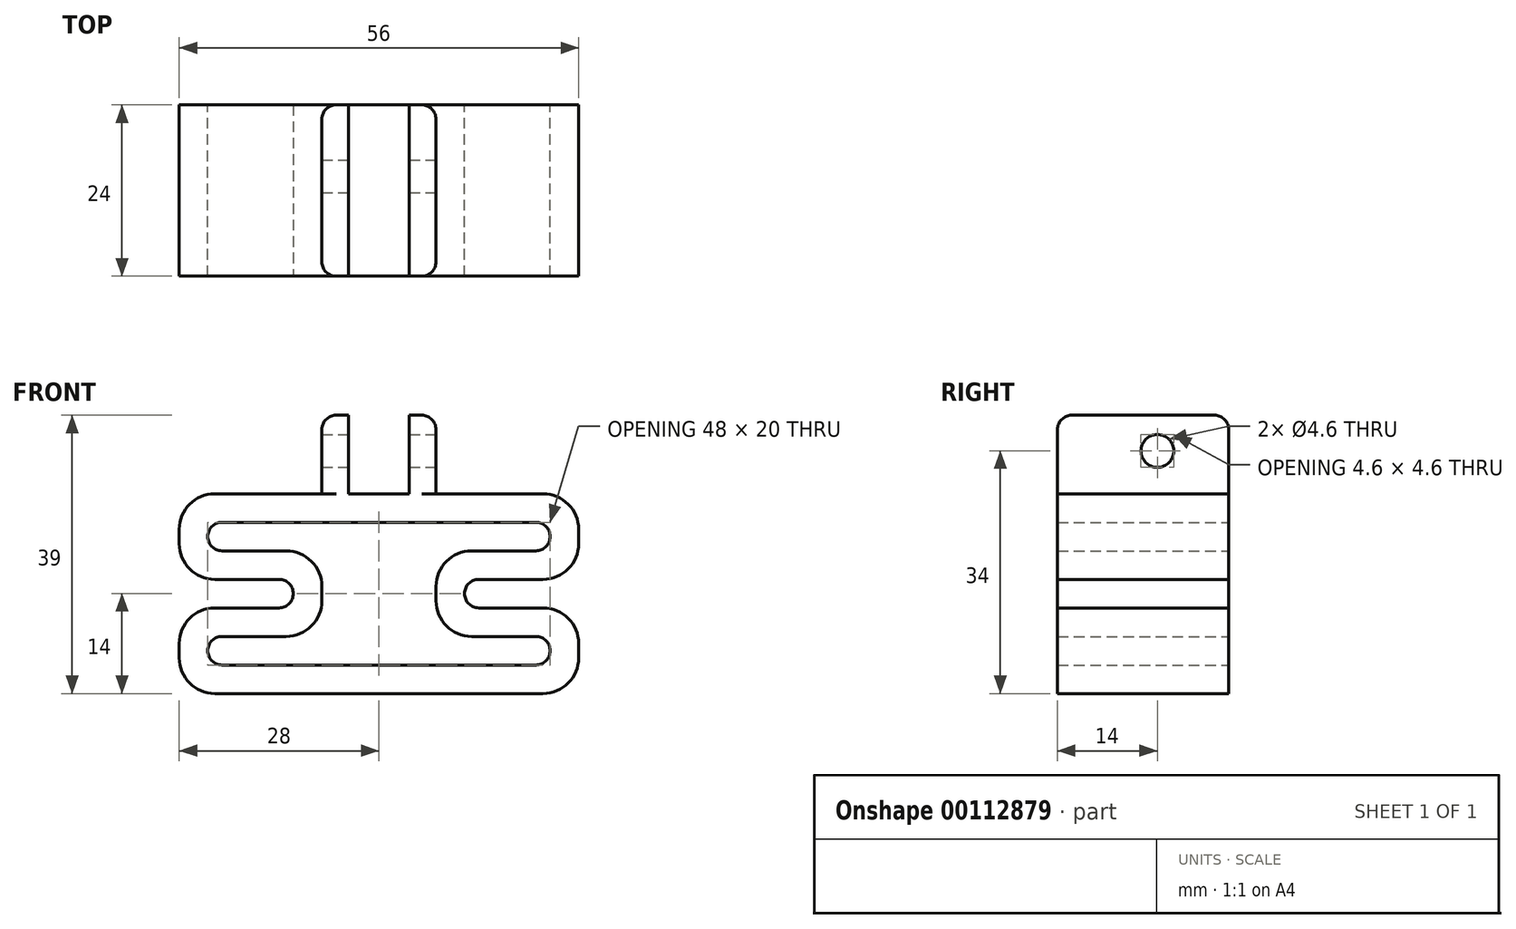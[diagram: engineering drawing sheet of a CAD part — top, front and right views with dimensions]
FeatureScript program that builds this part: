
annotation { "Feature Type Name" : "Feature", "Feature Type Description" : "" }
export const myFeature = defineFeature(function(context is Context, id is Id, definition is map)
    precondition{}
    {
        {
            var Q0;
            Q0=qCreatedBy(makeId("Front.planeOp"),FACE);
            var sketch = newSketch(context, id + "F0", { "sketchPlane" : qUnion([Q0])});
            skLineSegment(sketch, "E0.bottom", {"start": v(8, 11) * mm, "end": v(-8, 11) * mm});
            skLineSegment(sketch, "E0.left", {"start": v(8, 11) * mm, "end": v(8, -11) * mm});
            skLineSegment(sketch, "E0.right", {"start": v(-8, 11) * mm, "end": v(-8, 0) * mm});
            skPoint(sketch, "E0.middle", {"position": v(0, 0) * mm});
            skLineSegment(sketch, "E1.bottom", {"start": v(0, 0) * mm, "end": v(-28, 0) * mm});
            skLineSegment(sketch, "E1.top", {"start": v(0, -28) * mm, "end": v(-28, -28) * mm});
            skLineSegment(sketch, "E1.left", {"start": v(0, 0) * mm, "end": v(0, -28) * mm});
            skLineSegment(sketch, "E1.right", {"start": v(-28, 0) * mm, "end": v(-28, -12) * mm});
            skLineSegment(sketch, "E2", {"start": v(-8, -8) * mm, "end": v(-8, -20) * mm, "construction": true});
            skLineSegment(sketch, "E3.bottom", {"start": v(-8, -4) * mm, "end": v(-24, -4) * mm});
            skLineSegment(sketch, "E3.top", {"start": v(-8, -8) * mm, "end": v(-24, -8) * mm});
            skLineSegment(sketch, "E3.left", {"start": v(-8, -4) * mm, "end": v(-8, -8) * mm});
            skLineSegment(sketch, "E3.right", {"start": v(-24, -4) * mm, "end": v(-24, -8) * mm});
            skLineSegment(sketch, "E4.bottom", {"start": v(-28, -12) * mm, "end": v(-12, -12) * mm});
            skLineSegment(sketch, "E4.top", {"start": v(-28, -16) * mm, "end": v(-12, -16) * mm});
            skLineSegment(sketch, "E4.right", {"start": v(-12, -12) * mm, "end": v(-12, -16) * mm});
            skLineSegment(sketch, "E5.bottom", {"start": v(-8, -20) * mm, "end": v(-24, -20) * mm});
            skLineSegment(sketch, "E5.top", {"start": v(-8, -24) * mm, "end": v(-24, -24) * mm});
            skLineSegment(sketch, "E5.left", {"start": v(-8, -20) * mm, "end": v(-8, -24) * mm});
            skLineSegment(sketch, "E5.right", {"start": v(-24, -20) * mm, "end": v(-24, -24) * mm});
            skLineSegment(sketch, "E6.MirrorCS", {"start": v(0, 0) * mm, "end": v(28, 0) * mm});
            skLineSegment(sketch, "E7.MirrorCS", {"start": v(28, 0) * mm, "end": v(28, -12) * mm});
            skLineSegment(sketch, "E8.MirrorCS", {"start": v(28, -12) * mm, "end": v(12, -12) * mm});
            skLineSegment(sketch, "E9.MirrorCS", {"start": v(12, -12) * mm, "end": v(12, -16) * mm});
            skLineSegment(sketch, "E10.MirrorCS", {"start": v(28, -16) * mm, "end": v(12, -16) * mm});
            skLineSegment(sketch, "E11.MirrorCS", {"start": v(8, -20) * mm, "end": v(24, -20) * mm});
            skLineSegment(sketch, "E12.MirrorCS", {"start": v(24, -20) * mm, "end": v(24, -24) * mm});
            skLineSegment(sketch, "E13.MirrorCS", {"start": v(8, -24) * mm, "end": v(24, -24) * mm});
            skLineSegment(sketch, "E14.MirrorCS", {"start": v(0, -28) * mm, "end": v(28, -28) * mm});
            skLineSegment(sketch, "E15.MirrorCS", {"start": v(8, -4) * mm, "end": v(24, -4) * mm});
            skLineSegment(sketch, "E16.MirrorCS", {"start": v(24, -4) * mm, "end": v(24, -8) * mm});
            skLineSegment(sketch, "E17.MirrorCS", {"start": v(8, -8) * mm, "end": v(24, -8) * mm});
            skLineSegment(sketch, "E18.MirrorCS", {"start": v(8, -8) * mm, "end": v(8, -20) * mm, "construction": true});
            skLineSegment(sketch, "E19", {"start": v(-8, -4) * mm, "end": v(8, -4) * mm});
            skLineSegment(sketch, "E20", {"start": v(-8, -11) * mm, "end": v(-8, -20) * mm});
            skLineSegment(sketch, "E21", {"start": v(-8, -24) * mm, "end": v(8, -24) * mm});
            skLineSegment(sketch, "E22", {"start": v(8, -20) * mm, "end": v(8, -11) * mm});
            skPoint(sketch, "E23.orphan", {"position": v(-8, 0) * mm});
            skLineSegment(sketch, "E24.trimOffspring", {"start": v(-8, -24) * mm, "end": v(-8, -28) * mm, "construction": true});
            skLineSegment(sketch, "E25.trimOffspring", {"start": v(8, -24) * mm, "end": v(8, -28) * mm, "construction": true});
            skLineSegment(sketch, "E26.trimOffspring", {"start": v(-8, -4) * mm, "end": v(-8, -11) * mm});
            skPoint(sketch, "E27.orphan", {"position": v(8, 0) * mm});
            skLineSegment(sketch, "E28.trimOffspring", {"start": v(-28, -16) * mm, "end": v(-28, -28) * mm});
            skLineSegment(sketch, "E29.trimOffspring", {"start": v(28, -16) * mm, "end": v(28, -28) * mm});
            skLineSegment(sketch, "E30.bottom", {"start": v(-4.25, 0) * mm, "end": v(4.25, 0) * mm});
            skLineSegment(sketch, "E30.top", {"start": v(-4.25, 22) * mm, "end": v(4.25, 22) * mm});
            skLineSegment(sketch, "E30.left", {"start": v(-4.25, 0) * mm, "end": v(-4.25, 22) * mm});
            skLineSegment(sketch, "E30.right", {"start": v(4.25, 0) * mm, "end": v(4.25, 22) * mm});
            skPoint(sketch, "E30.middle", {"position": v(0, 11) * mm});
            skSolve(sketch);
        }
        {
            var Q0;
            {var subQ0=sQuery(id+"F0.wireOp",EDGE,"E1.top");Q0=makeQuery(id+"F0.imprint","IMPRINT",FACE,{"disambiguationData":[TD([[makeQuery(id+"F0.imprint","IMPRINT",EDGE,{"derivedFrom":subQ0}),-1.0]])]});}
            var Q1;
            {var subQ7=sQuery(id+"F0.wireOp",EDGE,"E7.MirrorCS");Q1=makeQuery(id+"F0.imprint","IMPRINT",FACE,{"disambiguationData":[TD([[makeQuery(id+"F0.imprint","IMPRINT",EDGE,{"derivedFrom":subQ7}),-1.0]])]});}
            var Q2;
            {var subQ1=sQuery(id+"F0.wireOp",EDGE,"E0.left");var subQ3=sQuery(id+"F0.wireOp",EDGE,"E6.MirrorCS");var subQ4=makeQuery(id+"F0.imprint","INTERSECT",VERTEX,{"derivedFrom":[subQ1,subQ3]});Q2=makeQuery(id+"F0.imprint","IMPRINT",FACE,{"disambiguationData":[TD([[makeQuery(id+"F0.imprint","IMPRINT",EDGE,{"disambiguationData":[TD([[subQ4,-1.0]])],"derivedFrom":subQ1}),-1.0]])]});}
            var Q3;
            {var subQ5=sQuery(id+"F0.wireOp",EDGE,"E0.bottom");Q3=makeQuery(id+"F0.imprint","IMPRINT",FACE,{"disambiguationData":[TD([[makeQuery(id+"F0.imprint","IMPRINT",EDGE,{"derivedFrom":subQ5}),1.0]])]});}
            var Q4;
            {var subQ3=sQuery(id+"F0.wireOp",EDGE,"E0.bottom");var subQ6=sQuery(id+"F0.wireOp",EDGE,"E30.right");var subQ8=makeQuery(id+"F0.imprint","INTERSECT",VERTEX,{"derivedFrom":[subQ3,subQ6]});Q4=makeQuery(id+"F0.imprint","IMPRINT",FACE,{"disambiguationData":[TD([[makeQuery(id+"F0.imprint","IMPRINT",EDGE,{"disambiguationData":[TD([[subQ8,-1.0]])],"derivedFrom":subQ3}),1.0]])]});}
            extrude(context, id + "F1", {"entities" : qUnion([Q0, Q1, Q2, Q3, Q4]), "depth" : 24 * mm});
        }
        {
            var Q0;
            Q0=makeQuery(id+"F1.opExtrude","SWEPT_FACE",FACE,{"disambiguationData":[OSD([sQuery(id+"F0.wireOp",EDGE,"E0.left")])]});
            var sketch = newSketch(context, id + "F2", { "sketchPlane" : qUnion([Q0])});
            skPoint(sketch, "E31", {"position": v(-10, 6) * mm});
            skSolve(sketch);
        }
        {
            var Q0;
            {var subQ3=sQuery(id+"F0.wireOp",EDGE,"E0.bottom");var subQ6=sQuery(id+"F0.wireOp",EDGE,"E30.right");var subQ8=makeQuery(id+"F0.imprint","INTERSECT",VERTEX,{"derivedFrom":[subQ3,subQ6]});Q0=makeQuery(id+"F0.imprint","IMPRINT",FACE,{"disambiguationData":[TD([[makeQuery(id+"F0.imprint","IMPRINT",EDGE,{"disambiguationData":[TD([[subQ8,-1.0]])],"derivedFrom":subQ3}),1.0]])]});}
            extrude(context, id + "F3", {"entities" : qUnion([Q0]), "operationType" : NewBodyOperationType.REMOVE, "endBound" : BoundingType.THROUGH_ALL, "depth" : 20 * mm});
        }
        {
            var Q0;
            Q0=sQuery(id+"F2.wireOp",VERTEX,"E31");
            var Q1;
            Q1=makeQuery(id+"F1.opExtrude","SWEPT_BODY",BODY,{"disambiguationData":[OSD([sQuery(id+"F0.wireOp",EDGE,"E0.bottom"),sQuery(id+"F0.wireOp",EDGE,"E0.left"),sQuery(id+"F0.wireOp",EDGE,"E0.right"),sQuery(id+"F0.wireOp",EDGE,"E1.bottom"),sQuery(id+"F0.wireOp",EDGE,"E1.top"),sQuery(id+"F0.wireOp",EDGE,"E1.right"),sQuery(id+"F0.wireOp",EDGE,"E3.bottom"),sQuery(id+"F0.wireOp",EDGE,"E3.top"),sQuery(id+"F0.wireOp",EDGE,"E3.right"),sQuery(id+"F0.wireOp",EDGE,"E4.bottom"),sQuery(id+"F0.wireOp",EDGE,"E4.top"),sQuery(id+"F0.wireOp",EDGE,"E4.right"),sQuery(id+"F0.wireOp",EDGE,"E5.bottom"),sQuery(id+"F0.wireOp",EDGE,"E5.top"),sQuery(id+"F0.wireOp",EDGE,"E5.right"),sQuery(id+"F0.wireOp",EDGE,"E6.MirrorCS"),sQuery(id+"F0.wireOp",EDGE,"E7.MirrorCS"),sQuery(id+"F0.wireOp",EDGE,"E8.MirrorCS"),sQuery(id+"F0.wireOp",EDGE,"E9.MirrorCS"),sQuery(id+"F0.wireOp",EDGE,"E10.MirrorCS"),sQuery(id+"F0.wireOp",EDGE,"E11.MirrorCS"),sQuery(id+"F0.wireOp",EDGE,"E12.MirrorCS"),sQuery(id+"F0.wireOp",EDGE,"E13.MirrorCS"),sQuery(id+"F0.wireOp",EDGE,"E14.MirrorCS"),sQuery(id+"F0.wireOp",EDGE,"E15.MirrorCS"),sQuery(id+"F0.wireOp",EDGE,"E16.MirrorCS"),sQuery(id+"F0.wireOp",EDGE,"E17.MirrorCS"),sQuery(id+"F0.wireOp",EDGE,"E19"),sQuery(id+"F0.wireOp",EDGE,"E20"),sQuery(id+"F0.wireOp",EDGE,"E21"),sQuery(id+"F0.wireOp",EDGE,"E22"),sQuery(id+"F0.wireOp",EDGE,"E26.trimOffspring"),sQuery(id+"F0.wireOp",EDGE,"E28.trimOffspring"),sQuery(id+"F0.wireOp",EDGE,"E29.trimOffspring")])]});
            hole(context, id + "F4", {"style" : HoleStyle.SIMPLE, "endStyle" : HoleEndStyle.THROUGH, "holeDiameter" : 4.6 * mm, "startFromSketch" : true, "locations" : qUnion([Q0]), "scope" : qUnion([Q1]), "isTappedThrough" : true});
        }
        {
            var Q0;
            Q0=makeQuery(id+"F1.opExtrude","SWEPT_EDGE",EDGE,{"disambiguationData":[OSD([sQuery(id+"F0.wireOp",EDGE,"E9.MirrorCS"),sQuery(id+"F0.wireOp",EDGE,"E10.MirrorCS")])]});
            var Q1;
            Q1=makeQuery(id+"F1.opExtrude","SWEPT_EDGE",EDGE,{"disambiguationData":[OSD([sQuery(id+"F0.wireOp",EDGE,"E5.top"),sQuery(id+"F0.wireOp",EDGE,"E5.right")])]});
            var Q2;
            Q2=makeQuery(id+"F1.opExtrude","SWEPT_EDGE",EDGE,{"disambiguationData":[OSD([sQuery(id+"F0.wireOp",EDGE,"E3.top"),sQuery(id+"F0.wireOp",EDGE,"E3.right")])]});
            var Q3;
            Q3=makeQuery(id+"F1.opExtrude","SWEPT_EDGE",EDGE,{"disambiguationData":[OSD([sQuery(id+"F0.wireOp",EDGE,"E8.MirrorCS"),sQuery(id+"F0.wireOp",EDGE,"E9.MirrorCS")])]});
            var Q4;
            Q4=makeQuery(id+"F1.opExtrude","SWEPT_EDGE",EDGE,{"disambiguationData":[OSD([sQuery(id+"F0.wireOp",EDGE,"E16.MirrorCS"),sQuery(id+"F0.wireOp",EDGE,"E17.MirrorCS")])]});
            var Q5;
            Q5=makeQuery(id+"F1.opExtrude","SWEPT_EDGE",EDGE,{"disambiguationData":[OSD([sQuery(id+"F0.wireOp",EDGE,"E12.MirrorCS"),sQuery(id+"F0.wireOp",EDGE,"E13.MirrorCS")])]});
            var Q6;
            Q6=makeQuery(id+"F1.opExtrude","SWEPT_EDGE",EDGE,{"disambiguationData":[OSD([sQuery(id+"F0.wireOp",EDGE,"E4.bottom"),sQuery(id+"F0.wireOp",EDGE,"E4.right")])]});
            var Q7;
            Q7=makeQuery(id+"F1.opExtrude","SWEPT_EDGE",EDGE,{"disambiguationData":[OSD([sQuery(id+"F0.wireOp",EDGE,"E11.MirrorCS"),sQuery(id+"F0.wireOp",EDGE,"E12.MirrorCS")])]});
            var Q8;
            Q8=makeQuery(id+"F1.opExtrude","SWEPT_EDGE",EDGE,{"disambiguationData":[OSD([sQuery(id+"F0.wireOp",EDGE,"E15.MirrorCS"),sQuery(id+"F0.wireOp",EDGE,"E16.MirrorCS")])]});
            var Q9;
            Q9=makeQuery(id+"F1.opExtrude","SWEPT_EDGE",EDGE,{"disambiguationData":[OSD([sQuery(id+"F0.wireOp",EDGE,"E5.bottom"),sQuery(id+"F0.wireOp",EDGE,"E5.right")])]});
            var Q10;
            Q10=makeQuery(id+"F1.opExtrude","SWEPT_EDGE",EDGE,{"disambiguationData":[OSD([sQuery(id+"F0.wireOp",EDGE,"E3.bottom"),sQuery(id+"F0.wireOp",EDGE,"E3.right")])]});
            var Q11;
            Q11=makeQuery(id+"F1.opExtrude","SWEPT_EDGE",EDGE,{"disambiguationData":[OSD([sQuery(id+"F0.wireOp",EDGE,"E4.top"),sQuery(id+"F0.wireOp",EDGE,"E4.right")])]});
            var Q12;
            Q12=makeQuery(id+"F1.opExtrude","SWEPT_EDGE",EDGE,{"disambiguationData":[OSD([sQuery(id+"F0.wireOp",EDGE,"E0.bottom"),sQuery(id+"F0.wireOp",EDGE,"E0.right")])]});
            var Q13;
            Q13=makeQuery(id+"F1.opExtrude","CAP_EDGE",EDGE,{"disambiguationData":[OSD([sQuery(id+"F0.wireOp",EDGE,"E0.bottom")])],"isStart":false});
            var Q14;
            Q14=makeQuery(id+"F1.opExtrude","SWEPT_EDGE",EDGE,{"disambiguationData":[OSD([sQuery(id+"F0.wireOp",EDGE,"E0.bottom"),sQuery(id+"F0.wireOp",EDGE,"E0.left")])]});
            var Q15;
            Q15=makeQuery(id+"F1.opExtrude","CAP_EDGE",EDGE,{"disambiguationData":[OSD([sQuery(id+"F0.wireOp",EDGE,"E0.right")])],"isStart":true});
            var Q16;
            Q16=makeQuery(id+"F1.opExtrude","CAP_EDGE",EDGE,{"disambiguationData":[OSD([sQuery(id+"F0.wireOp",EDGE,"E0.right")])],"isStart":false});
            var Q17;
            {var subQ0=sQuery(id+"F0.wireOp",EDGE,"E0.bottom");var subQ1=sQuery(id+"F0.wireOp",EDGE,"E0.right");Q17=makeQuery(id+"F3.boolean.opBoolean","SPLIT",EDGE,{"disambiguationData":[TD([makeQuery(id+"F1.opExtrude","SWEPT_FACE",FACE,{"disambiguationData":[OSD([subQ1])]})])],"derivedFrom":makeQuery(id+"F1.opExtrude","CAP_EDGE",EDGE,{"disambiguationData":[OSD([subQ0])],"isStart":true})});}
            var Q18;
            {var subQ0=sQuery(id+"F0.wireOp",EDGE,"E0.bottom");var subQ1=sQuery(id+"F0.wireOp",EDGE,"E0.left");Q18=makeQuery(id+"F3.boolean.opBoolean","SPLIT",EDGE,{"disambiguationData":[TD([makeQuery(id+"F1.opExtrude","SWEPT_FACE",FACE,{"disambiguationData":[OSD([subQ1])]})])],"derivedFrom":makeQuery(id+"F1.opExtrude","CAP_EDGE",EDGE,{"disambiguationData":[OSD([subQ0])],"isStart":true})});}
            var Q19;
            Q19=makeQuery(id+"F1.opExtrude","CAP_EDGE",EDGE,{"disambiguationData":[OSD([sQuery(id+"F0.wireOp",EDGE,"E0.left")])],"isStart":true});
            var Q20;
            Q20=makeQuery(id+"F1.opExtrude","CAP_EDGE",EDGE,{"disambiguationData":[OSD([sQuery(id+"F0.wireOp",EDGE,"E0.left")])],"isStart":false});
            fillet(context, id + "F5", {"entities" : qUnion([Q0, Q1, Q2, Q3, Q4, Q5, Q6, Q7, Q8, Q9, Q10, Q11, Q12, Q13, Q14, Q15, Q16, Q17, Q18, Q19, Q20]), "radius" : 2 * mm, "tangentPropagation" : true, "allowEdgeOverflow" : false});
        }
        {
            var Q0;
            Q0=makeQuery(id+"F1.opExtrude","SWEPT_EDGE",EDGE,{"disambiguationData":[OSD([sQuery(id+"F0.wireOp",EDGE,"E1.top"),sQuery(id+"F0.wireOp",EDGE,"E28.trimOffspring")])]});
            var Q1;
            Q1=makeQuery(id+"F1.opExtrude","SWEPT_EDGE",EDGE,{"disambiguationData":[OSD([sQuery(id+"F0.wireOp",EDGE,"E4.top"),sQuery(id+"F0.wireOp",EDGE,"E28.trimOffspring")])]});
            var Q2;
            Q2=makeQuery(id+"F1.opExtrude","SWEPT_EDGE",EDGE,{"disambiguationData":[OSD([sQuery(id+"F0.wireOp",EDGE,"E1.right"),sQuery(id+"F0.wireOp",EDGE,"E4.bottom")])]});
            var Q3;
            Q3=makeQuery(id+"F1.opExtrude","SWEPT_EDGE",EDGE,{"disambiguationData":[OSD([sQuery(id+"F0.wireOp",EDGE,"E1.bottom"),sQuery(id+"F0.wireOp",EDGE,"E1.right")])]});
            var Q4;
            Q4=makeQuery(id+"F1.opExtrude","SWEPT_EDGE",EDGE,{"disambiguationData":[OSD([sQuery(id+"F0.wireOp",EDGE,"E0.left"),sQuery(id+"F0.wireOp",EDGE,"E17.MirrorCS")])]});
            var Q5;
            Q5=makeQuery(id+"F1.opExtrude","SWEPT_EDGE",EDGE,{"disambiguationData":[OSD([sQuery(id+"F0.wireOp",EDGE,"E11.MirrorCS"),sQuery(id+"F0.wireOp",EDGE,"E22")])]});
            var Q6;
            Q6=makeQuery(id+"F1.opExtrude","SWEPT_EDGE",EDGE,{"disambiguationData":[OSD([sQuery(id+"F0.wireOp",EDGE,"E3.top"),sQuery(id+"F0.wireOp",EDGE,"E26.trimOffspring")])]});
            var Q7;
            Q7=makeQuery(id+"F1.opExtrude","SWEPT_EDGE",EDGE,{"disambiguationData":[OSD([sQuery(id+"F0.wireOp",EDGE,"E5.bottom"),sQuery(id+"F0.wireOp",EDGE,"E5.left"),sQuery(id+"F0.wireOp",EDGE,"E20")])]});
            var Q8;
            Q8=makeQuery(id+"F1.opExtrude","SWEPT_EDGE",EDGE,{"disambiguationData":[OSD([sQuery(id+"F0.wireOp",EDGE,"E6.MirrorCS"),sQuery(id+"F0.wireOp",EDGE,"E7.MirrorCS")])]});
            var Q9;
            Q9=makeQuery(id+"F1.opExtrude","SWEPT_EDGE",EDGE,{"disambiguationData":[OSD([sQuery(id+"F0.wireOp",EDGE,"E7.MirrorCS"),sQuery(id+"F0.wireOp",EDGE,"E8.MirrorCS")])]});
            var Q10;
            Q10=makeQuery(id+"F1.opExtrude","SWEPT_EDGE",EDGE,{"disambiguationData":[OSD([sQuery(id+"F0.wireOp",EDGE,"E10.MirrorCS"),sQuery(id+"F0.wireOp",EDGE,"E29.trimOffspring")])]});
            var Q11;
            Q11=makeQuery(id+"F1.opExtrude","SWEPT_EDGE",EDGE,{"disambiguationData":[OSD([sQuery(id+"F0.wireOp",EDGE,"E14.MirrorCS"),sQuery(id+"F0.wireOp",EDGE,"E29.trimOffspring")])]});
            fillet(context, id + "F6", {"entities" : qUnion([Q0, Q1, Q2, Q3, Q4, Q5, Q6, Q7, Q8, Q9, Q10, Q11]), "radius" : 5 * mm, "tangentPropagation" : true, "allowEdgeOverflow" : false});
        }
    });
